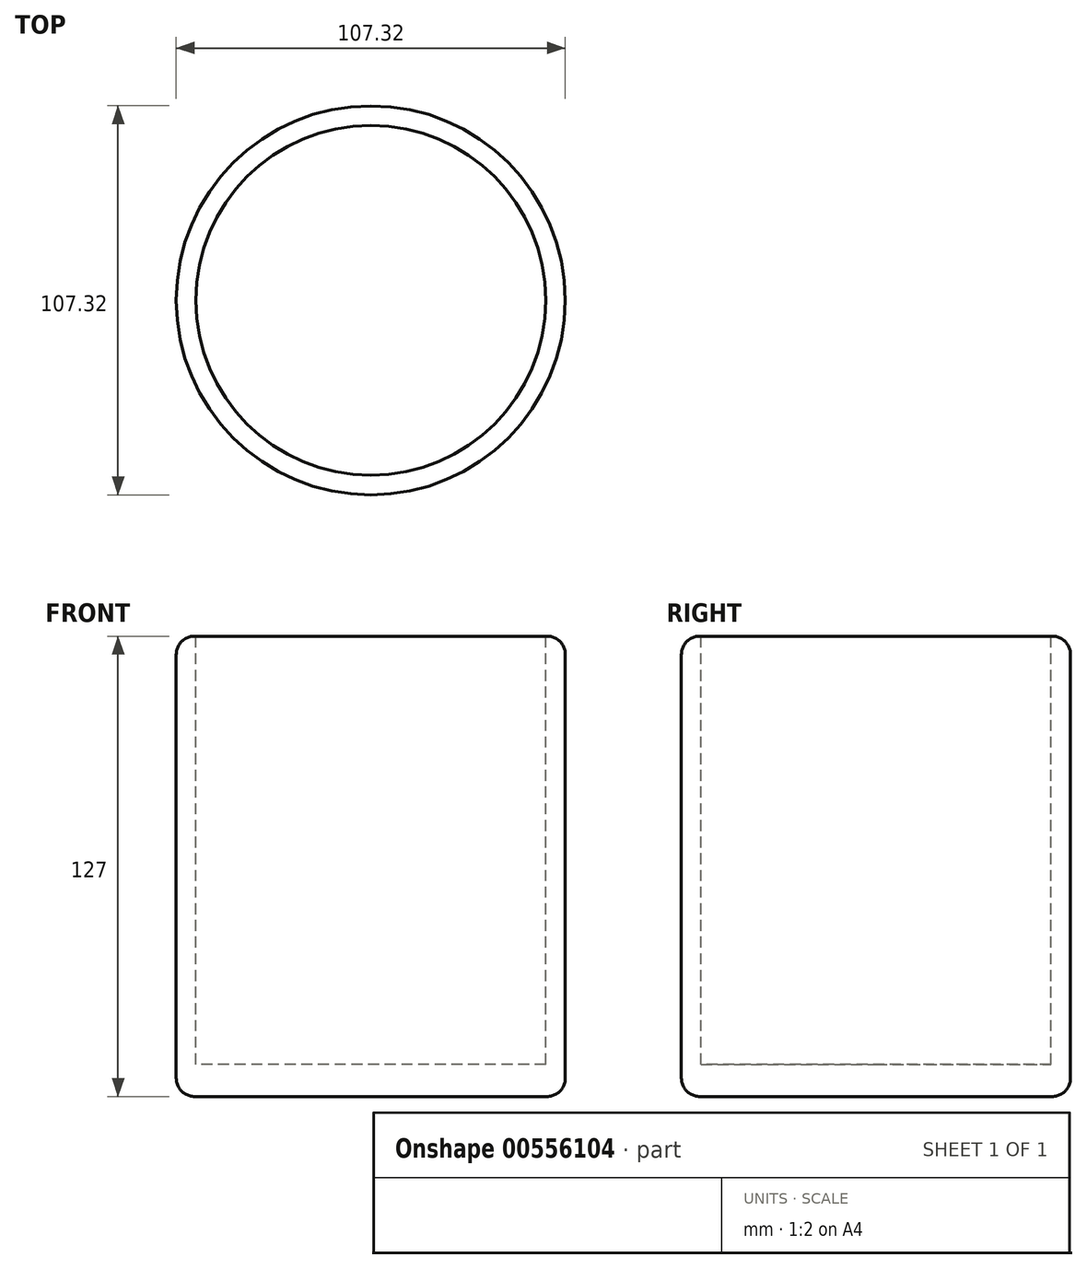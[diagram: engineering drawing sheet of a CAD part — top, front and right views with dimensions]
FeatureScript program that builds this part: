
annotation { "Feature Type Name" : "Feature", "Feature Type Description" : "" }
export const myFeature = defineFeature(function(context is Context, id is Id, definition is map)
    precondition{}
    {
        {
            var Q0;
            Q0=qCreatedBy(makeId("Top.planeOp"),FACE);
            var sketch = newSketch(context, id + "F0", { "sketchPlane" : qUnion([Q0])});
            skCircle(sketch, "E0", {"center": v(0, 0) * mm, "radius": 53.66 * mm});
            skSolve(sketch);
        }
        {
            var Q0;
            Q0 = qSketchRegion(id + "F0", true);
            extrude(context, id + "F1", {"entities" : qUnion([Q0]), "depth" : 127 * mm, "offsetDistance" : 25.4 * mm});
        }
        {
            var Q0;
            Q0=makeQuery(id+"F1.opExtrude","CAP_FACE",FACE,{"disambiguationData":[OSD([sQuery(id+"F0.wireOp",EDGE,"E0")])],"isStart":false});
            var sketch = newSketch(context, id + "F2", { "sketchPlane" : qUnion([Q0])});
            skCircle(sketch, "E1", {"center": v(0, 0) * mm, "radius": 48.26 * mm});
            skSolve(sketch);
        }
        {
            var Q0;
            Q0 = qSketchRegion(id + "F2", true);
            extrude(context, id + "F3", {"entities" : qUnion([Q0]), "operationType" : NewBodyOperationType.REMOVE, "oppositeDirection" : true, "depth" : 118.11 * mm, "offsetDistance" : 25.4 * mm});
        }
        {
            var Q0;
            Q0=makeQuery(id+"F1.opExtrude","CAP_EDGE",EDGE,{"disambiguationData":[OSD([sQuery(id+"F0.wireOp",EDGE,"E0")])],"isStart":false});
            fillet(context, id + "F4", {"entities" : qUnion([Q0]), "radius" : 5.08 * mm, "tangentPropagation" : true, "allowEdgeOverflow" : false});
        }
        {
            var Q0;
            Q0=makeQuery(id+"F1.opExtrude","CAP_EDGE",EDGE,{"disambiguationData":[OSD([sQuery(id+"F0.wireOp",EDGE,"E0")])],"isStart":true});
            fillet(context, id + "F5", {"entities" : qUnion([Q0]), "radius" : 5.08 * mm, "tangentPropagation" : true, "allowEdgeOverflow" : false});
        }
    });
